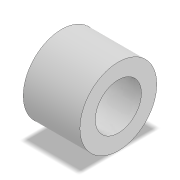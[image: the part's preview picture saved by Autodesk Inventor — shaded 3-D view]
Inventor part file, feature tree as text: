
AUTODESK INVENTOR PART (.ipt)
format: ipt  version: 2020 (Build 240168000, 168)  size: 84,992 bytes
history: native  units: in
note: dims shown in document units (in); Inventor stores cm internally (conversion verified against a paired STEP export)
features: extrude x1, sketch x1
ambient origin geometry x8: Origin, YZ Plane, XZ Plane, XY Plane, X Axis, Y Axis, Z Axis, Center Point
bodies: Solid1 (feature_tree)
feature tree (2):
  extrude  "Extrusion1"  Depth=0.2905in
  sketch  "Sketch1"  dims[d0=0.3937in d1=0.2362in d2=0.2905in d3=0.0in]
